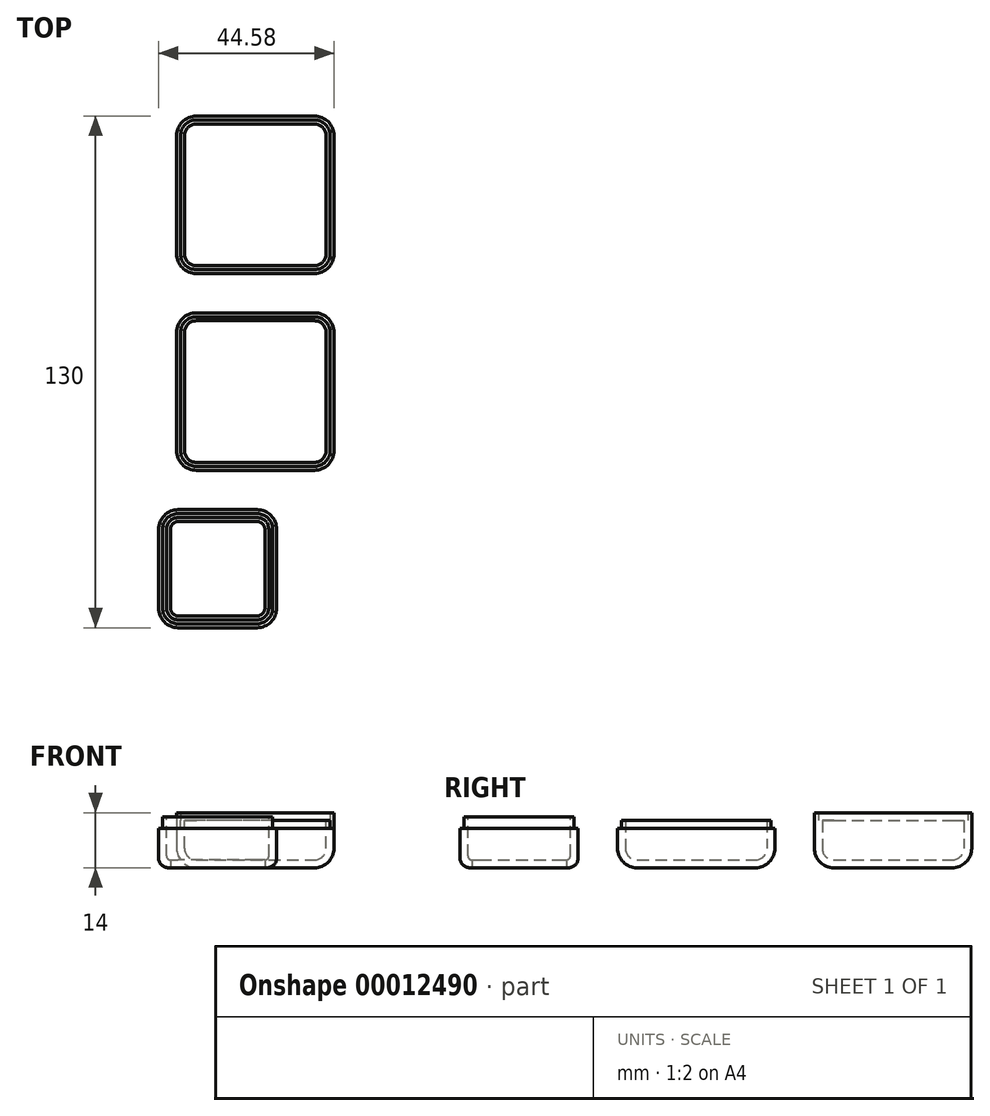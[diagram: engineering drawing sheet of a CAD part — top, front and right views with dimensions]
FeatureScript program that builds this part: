
annotation { "Feature Type Name" : "Feature", "Feature Type Description" : "" }
export const myFeature = defineFeature(function(context is Context, id is Id, definition is map)
    precondition{}
    {
        {
            var Q0;
            Q0=qCreatedBy(makeId("Top.planeOp"),FACE);
            var sketch = newSketch(context, id + "F0", { "sketchPlane" : qUnion([Q0])});
            skLineSegment(sketch, "E0.rect.bottom", {"start": v(20, -20) * mm, "end": v(-20, -20) * mm});
            skLineSegment(sketch, "E0.rect.top", {"start": v(20, 20) * mm, "end": v(-20, 20) * mm});
            skLineSegment(sketch, "E0.rect.left", {"start": v(20, -20) * mm, "end": v(20, 20) * mm});
            skLineSegment(sketch, "E0.rect.right", {"start": v(-20, -20) * mm, "end": v(-20, 20) * mm});
            skPoint(sketch, "E0.rect.middle", {"position": v(0, 0) * mm});
            skSolve(sketch);
        }
        {
            var Q0;
            Q0=makeQuery(id+"F0.imprint","IMPRINT",FACE,{"disambiguationData":[TD([[makeQuery(id+"F0.imprint","IMPRINT",EDGE,{"derivedFrom":sQuery(id+"F0.wireOp",EDGE,"E0.rect.bottom")}),-1.0]])]});
            extrude(context, id + "F1", {"entities" : qUnion([Q0]), "depth" : 12 * mm});
        }
        {
            var Q0;
            Q0=makeQuery(id+"F1.opExtrude","SWEPT_EDGE",EDGE,{"disambiguationData":[OSD([sQuery(id+"F0.wireOp",EDGE,"E0.rect.bottom"),sQuery(id+"F0.wireOp",EDGE,"E0.rect.left")])]});
            var Q1;
            Q1=makeQuery(id+"F1.opExtrude","SWEPT_EDGE",EDGE,{"disambiguationData":[OSD([sQuery(id+"F0.wireOp",EDGE,"E0.rect.top"),sQuery(id+"F0.wireOp",EDGE,"E0.rect.left")])]});
            var Q2;
            Q2=makeQuery(id+"F1.opExtrude","SWEPT_EDGE",EDGE,{"disambiguationData":[OSD([sQuery(id+"F0.wireOp",EDGE,"E0.rect.bottom"),sQuery(id+"F0.wireOp",EDGE,"E0.rect.right")])]});
            var Q3;
            Q3=makeQuery(id+"F1.opExtrude","SWEPT_EDGE",EDGE,{"disambiguationData":[OSD([sQuery(id+"F0.wireOp",EDGE,"E0.rect.top"),sQuery(id+"F0.wireOp",EDGE,"E0.rect.right")])]});
            var Q4;
            Q4=makeQuery(id+"F1.opExtrude","CAP_EDGE",EDGE,{"disambiguationData":[OSD([sQuery(id+"F0.wireOp",EDGE,"E0.rect.right")])],"isStart":true});
            var Q5;
            Q5=makeQuery(id+"F1.opExtrude","CAP_EDGE",EDGE,{"disambiguationData":[OSD([sQuery(id+"F0.wireOp",EDGE,"E0.rect.bottom")])],"isStart":true});
            var Q6;
            Q6=makeQuery(id+"F1.opExtrude","CAP_EDGE",EDGE,{"disambiguationData":[OSD([sQuery(id+"F0.wireOp",EDGE,"E0.rect.left")])],"isStart":true});
            var Q7;
            Q7=makeQuery(id+"F1.opExtrude","CAP_EDGE",EDGE,{"disambiguationData":[OSD([sQuery(id+"F0.wireOp",EDGE,"E0.rect.top")])],"isStart":true});
            fillet(context, id + "F2", {"entities" : qUnion([Q0, Q1, Q2, Q3, Q4, Q5, Q6, Q7]), "radius" : 5 * mm, "tangentPropagation" : true, "allowEdgeOverflow" : false});
        }
        {
            var Q0;
            Q0=makeQuery(id+"F1.opExtrude","CAP_FACE",FACE,{"disambiguationData":[OSD([sQuery(id+"F0.wireOp",EDGE,"E0.rect.bottom"),sQuery(id+"F0.wireOp",EDGE,"E0.rect.top"),sQuery(id+"F0.wireOp",EDGE,"E0.rect.left"),sQuery(id+"F0.wireOp",EDGE,"E0.rect.right")])],"isStart":false});
            shell(context, id + "F3", {"entities" : qUnion([Q0]), "thickness" : 2 * mm});
        }
        {
            var Q0;
            Q0=makeQuery(id+"F1.opExtrude","CAP_FACE",FACE,{"disambiguationData":[OSD([sQuery(id+"F0.wireOp",EDGE,"E0.rect.bottom"),sQuery(id+"F0.wireOp",EDGE,"E0.rect.top"),sQuery(id+"F0.wireOp",EDGE,"E0.rect.left"),sQuery(id+"F0.wireOp",EDGE,"E0.rect.right")])],"isStart":false});
            var sketch = newSketch(context, id + "F4", { "sketchPlane" : qUnion([Q0])});
            skArc(sketch, "E1.0", {"start": v(19, 15) * mm, "mid": v(17.83, 17.83) * mm, "end": v(15, 19) * mm});
            skLineSegment(sketch, "E1.1", {"start": v(19, -15) * mm, "end": v(19, 15) * mm});
            skArc(sketch, "E1.2", {"start": v(15, -19) * mm, "mid": v(17.83, -17.83) * mm, "end": v(19, -15) * mm});
            skLineSegment(sketch, "E1.3", {"start": v(15, -19) * mm, "end": v(-15, -19) * mm});
            skArc(sketch, "E1.4", {"start": v(-19, -15) * mm, "mid": v(-17.83, -17.83) * mm, "end": v(-15, -19) * mm});
            skLineSegment(sketch, "E1.5", {"start": v(15, 19) * mm, "end": v(-15, 19) * mm});
            skLineSegment(sketch, "E1.6", {"start": v(-19, -15) * mm, "end": v(-19, 15) * mm});
            skArc(sketch, "E1.7", {"start": v(-15, 19) * mm, "mid": v(-17.83, 17.83) * mm, "end": v(-19, 15) * mm});
            skSolve(sketch);
        }
        {
            var Q0;
            Q0=makeQuery(id+"F4.imprint","IMPRINT",FACE,{"disambiguationData":[TD([[makeQuery(id+"F4.imprint","IMPRINT",EDGE,{"derivedFrom":sQuery(id+"F4.wireOp",EDGE,"E1.0")}),-1.0]])]});
            extrude(context, id + "F5", {"entities" : qUnion([Q0]), "operationType" : NewBodyOperationType.REMOVE, "oppositeDirection" : true, "depth" : 2 * mm});
        }
        {
            var Q0;
            Q0=makeQuery(id+"F1.opExtrude","SWEPT_BODY",BODY,{"disambiguationData":[OSD([sQuery(id+"F0.wireOp",EDGE,"E0.rect.bottom"),sQuery(id+"F0.wireOp",EDGE,"E0.rect.top"),sQuery(id+"F0.wireOp",EDGE,"E0.rect.left"),sQuery(id+"F0.wireOp",EDGE,"E0.rect.right")])]});
            transform(context, id + "F6", {"entities" : qUnion([Q0]), "transformType" : TransformType.TRANSLATION_3D, "dx" : 0 * mm, "dy" : 50 * mm, "dz" : 0 * mm, "makeCopy" : true});
        }
        {
            var Q0;
            Q0=makeQuery(id+"F6.opPattern","COPY",FACE,{"derivedFrom":makeQuery(id+"F5.boolean.opBoolean","COPY",FACE,{"derivedFrom":makeQuery(id+"F5.opExtrude","CAP_FACE",FACE,{"disambiguationData":[OSD([sQuery(id+"F0.wireOp",EDGE,"E0.rect.bottom"),sQuery(id+"F0.wireOp",EDGE,"E0.rect.top"),sQuery(id+"F0.wireOp",EDGE,"E0.rect.left"),sQuery(id+"F0.wireOp",EDGE,"E0.rect.right"),sQuery(id+"F4.wireOp",EDGE,"E1.0"),sQuery(id+"F4.wireOp",EDGE,"E1.1"),sQuery(id+"F4.wireOp",EDGE,"E1.2"),sQuery(id+"F4.wireOp",EDGE,"E1.3"),sQuery(id+"F4.wireOp",EDGE,"E1.4"),sQuery(id+"F4.wireOp",EDGE,"E1.5"),sQuery(id+"F4.wireOp",EDGE,"E1.6"),sQuery(id+"F4.wireOp",EDGE,"E1.7")])],"isStart":false})}),"instanceName":"1"});
            extrude(context, id + "F7", {"entities" : qUnion([Q0]), "operationType" : NewBodyOperationType.ADD, "depth" : 4 * mm});
        }
        {
            var Q0;
            Q0=qCreatedBy(makeId("Right.planeOp"),FACE);
            var sketch = newSketch(context, id + "F8", { "sketchPlane" : qUnion([Q0])});
            skLineSegment(sketch, "E2", {"start": v(-32, 3) * mm, "end": v(-32, 13) * mm});
            skLineSegment(sketch, "E3", {"start": v(-32, 13) * mm, "end": v(-31, 13) * mm});
            skLineSegment(sketch, "E4", {"start": v(-31, 13) * mm, "end": v(-31, 10) * mm});
            skLineSegment(sketch, "E5", {"start": v(-31, 10) * mm, "end": v(-30, 10) * mm});
            skLineSegment(sketch, "E6", {"start": v(-30, 10) * mm, "end": v(-30, 2.5) * mm});
            skLineSegment(sketch, "E7.bottom", {"start": v(-32.5, 0) * mm, "end": v(-35, 0) * mm});
            skLineSegment(sketch, "E7.top", {"start": v(-33, 2) * mm, "end": v(-35, 2) * mm});
            skLineSegment(sketch, "E7.right", {"start": v(-35, 0) * mm, "end": v(-35, 2) * mm});
            skPoint(sketch, "E8.visualSharp", {"position": v(-30, 0) * mm});
            skArc(sketch, "E9.filletArc", {"start": v(-33, 2) * mm, "mid": v(-32.3, 2.3) * mm, "end": v(-32, 3) * mm});
            skArc(sketch, "E10.filletArc", {"start": v(-32.5, 0) * mm, "mid": v(-30.73, 0.73) * mm, "end": v(-30, 2.5) * mm});
            skLineSegment(sketch, "E11", {"start": v(-33, 2) * mm, "end": v(-33, 0) * mm});
            skSolve(sketch);
        }
        {
            var Q0;
            Q0=qCreatedBy(makeId("Top.planeOp"),FACE);
            var sketch = newSketch(context, id + "F9", { "sketchPlane" : qUnion([Q0])});
            skLineSegment(sketch, "E12.rect.bottom", {"start": v(0.42, -60) * mm, "end": v(-19.58, -60) * mm});
            skLineSegment(sketch, "E12.rect.top", {"start": v(0.42, -30) * mm, "end": v(-19.58, -30) * mm});
            skLineSegment(sketch, "E12.rect.left", {"start": v(5.42, -55) * mm, "end": v(5.42, -35) * mm});
            skLineSegment(sketch, "E12.rect.right", {"start": v(-24.58, -55) * mm, "end": v(-24.58, -35) * mm});
            skPoint(sketch, "E12.rect.middle", {"position": v(-9.58, -45) * mm});
            skPoint(sketch, "E13.visualSharp", {"position": v(5.42, -60) * mm});
            skArc(sketch, "E13.filletArc", {"start": v(0.42, -60) * mm, "mid": v(3.95, -58.54) * mm, "end": v(5.42, -55) * mm});
            skPoint(sketch, "E14.visualSharp", {"position": v(-24.58, -60) * mm});
            skArc(sketch, "E14.filletArc", {"start": v(-24.58, -55) * mm, "mid": v(-23.12, -58.54) * mm, "end": v(-19.58, -60) * mm});
            skPoint(sketch, "E15.visualSharp", {"position": v(-24.58, -30) * mm});
            skArc(sketch, "E15.filletArc", {"start": v(-19.58, -30) * mm, "mid": v(-23.12, -31.46) * mm, "end": v(-24.58, -35) * mm});
            skPoint(sketch, "E16.visualSharp", {"position": v(5.42, -30) * mm});
            skArc(sketch, "E16.filletArc", {"start": v(5.42, -35) * mm, "mid": v(3.95, -31.46) * mm, "end": v(0.42, -30) * mm});
            skSolve(sketch);
        }
        {
            var Q0;
            Q0=makeQuery(id+"F8.imprint","IMPRINT",FACE,{"disambiguationData":[TD([[makeQuery(id+"F8.imprint","IMPRINT",EDGE,{"derivedFrom":sQuery(id+"F8.wireOp",EDGE,"E2")}),-1.0]])]});
            var Q1;
            Q1=sQuery(id+"F9.wireOp",EDGE,"E12.rect.bottom");
            var Q2;
            Q2=sQuery(id+"F9.wireOp",EDGE,"E12.rect.right");
            var Q3;
            Q3=sQuery(id+"F9.wireOp",EDGE,"E12.rect.top");
            var Q4;
            Q4=sQuery(id+"F9.wireOp",EDGE,"E12.rect.left");
            var Q5;
            Q5=sQuery(id+"F9.wireOp",EDGE,"E14.filletArc");
            var Q6;
            Q6=sQuery(id+"F9.wireOp",EDGE,"E13.filletArc");
            var Q7;
            Q7=sQuery(id+"F9.wireOp",EDGE,"E16.filletArc");
            var Q8;
            Q8=sQuery(id+"F9.wireOp",EDGE,"E15.filletArc");
            sweep(context, id + "F10", {"profiles" : qUnion([Q0]), "path" : qUnion([Q1, Q2, Q3, Q4, Q5, Q6, Q7, Q8])});
        }
    });
